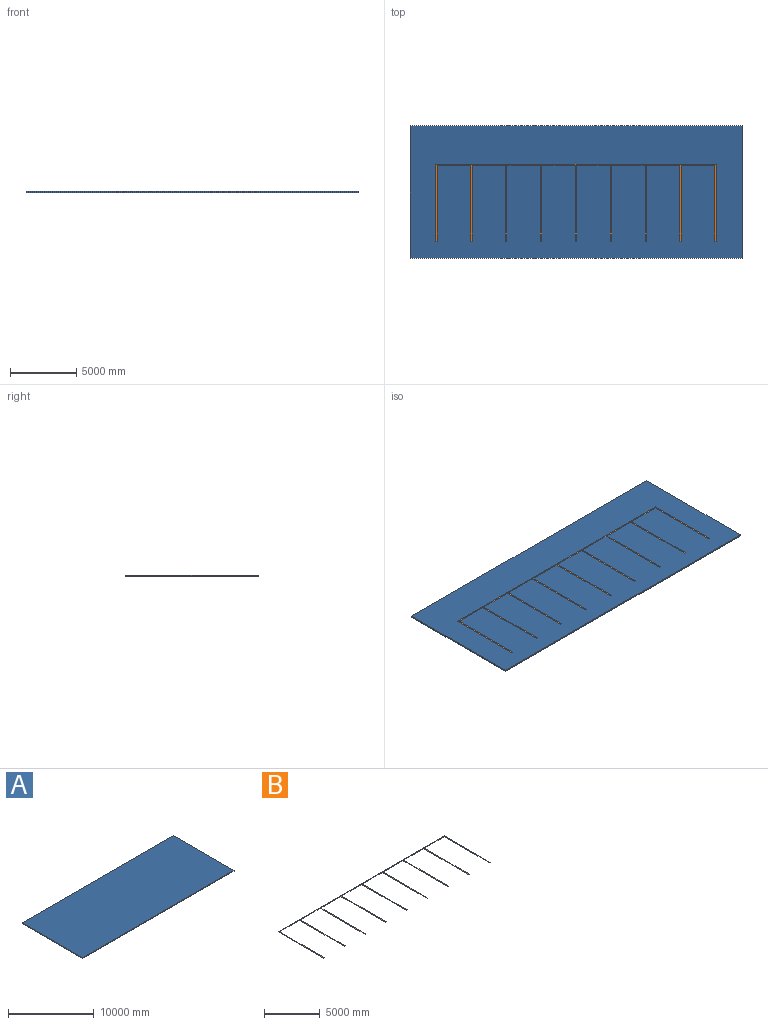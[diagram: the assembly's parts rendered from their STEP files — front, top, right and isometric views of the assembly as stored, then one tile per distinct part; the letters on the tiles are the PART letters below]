
ASSEMBLY  parts=2 mates=1
PART A: 6 faces, bbox 25000x10000x100 mm
  f0: plane 10000x100mm, normal (1,0,0), area 1000000mm2, adj f1,f3,f4,f5
  f1: plane 25000x100mm, normal (0,1,0), area 2500000mm2, adj f0,f2,f4,f5
  f2: plane 10000x100mm, normal (-1,0,0), area 1000000mm2, adj f1,f3,f4,f5
  f3: plane 25000x100mm, normal (0,-1,0), area 2500000mm2, adj f0,f2,f4,f5
  f4: plane 25000x10000mm, normal (0,0,1), area 250000000mm2, adj f0,f1,f2,f3
  f5: plane 25000x10000mm, normal (0,0,-1), area 250000000mm2, adj f0,f1,f2,f3
PART B: 38 faces, bbox 21100x5800x0.3 mm
  f0: plane 5800x0.25mm, normal (1,0,0), area 1450mm2, adj f1,f35,f36,f37
  f1: plane 21100x0.25mm, normal (0,1,0), area 5275mm2, adj f0,f2,f36,f37
  f2: plane 5800x0.25mm, normal (-1,0,0), area 1450mm2, adj f1,f3,f36,f37
  f3: plane 100x0.25mm, normal (0,-1,0), area 25mm2, adj f2,f4,f36,f37
  f4: plane 5700x0.25mm, normal (1,0,0), area 1425mm2, adj f3,f5,f36,f37
  f5: plane 2525x0.25mm, normal (0,-1,0), area 631.2mm2, adj f4,f6,f36,f37
  f6: plane 5700x0.25mm, normal (-1,0,0), area 1425mm2, adj f5,f7,f36,f37
  f7: plane 100x0.25mm, normal (0,-1,0), area 25mm2, adj f6,f8,f36,f37
  f8: plane 5700x0.25mm, normal (1,0,0), area 1425mm2, adj f7,f9,f36,f37
  f9: plane 2525x0.25mm, normal (0,-1,0), area 631.3mm2, adj f8,f10,f36,f37
  f10: plane 5700x0.25mm, normal (-1,0,0), area 1425mm2, adj f9,f11,f36,f37
  f11: plane 100x0.25mm, normal (0,-1,0), area 25mm2, adj f10,f12,f36,f37
  f12: plane 5700x0.25mm, normal (1,0,0), area 1425mm2, adj f11,f13,f36,f37
  f13: plane 2525x0.25mm, normal (0,-1,0), area 631.3mm2, adj f12,f14,f36,f37
  f14: plane 5700x0.25mm, normal (-1,0,0), area 1425mm2, adj f13,f15,f36,f37
  f15: plane 100x0.25mm, normal (0,-1,0), area 25mm2, adj f14,f16,f36,f37
  f16: plane 5700x0.25mm, normal (1,0,0), area 1425mm2, adj f15,f17,f36,f37
  f17: plane 2525x0.25mm, normal (0,-1,0), area 631.3mm2, adj f16,f18,f36,f37
  f18: plane 5700x0.25mm, normal (-1,0,0), area 1425mm2, adj f17,f19,f36,f37
  f19: plane 100x0.25mm, normal (0,-1,0), area 25mm2, adj f18,f20,f36,f37
  f20: plane 5700x0.25mm, normal (1,0,0), area 1425mm2, adj f19,f21,f36,f37
  f21: plane 2525x0.25mm, normal (0,-1,0), area 631.3mm2, adj f20,f22,f36,f37
  f22: plane 5700x0.25mm, normal (-1,0,0), area 1425mm2, adj f21,f23,f36,f37
  f23: plane 100x0.25mm, normal (0,-1,0), area 25mm2, adj f22,f24,f36,f37
  f24: plane 5700x0.25mm, normal (1,0,0), area 1425mm2, adj f23,f25,f36,f37
  f25: plane 2525x0.25mm, normal (0,-1,0), area 631.3mm2, adj f24,f26,f36,f37
  f26: plane 5700x0.25mm, normal (-1,0,0), area 1425mm2, adj f25,f27,f36,f37
  f27: plane 100x0.25mm, normal (0,-1,0), area 25mm2, adj f26,f28,f36,f37
  f28: plane 5700x0.25mm, normal (1,0,0), area 1425mm2, adj f27,f29,f36,f37
  f29: plane 2525x0.25mm, normal (0,-1,0), area 631.3mm2, adj f28,f30,f36,f37
  f30: plane 5700x0.25mm, normal (-1,0,0), area 1425mm2, adj f29,f31,f36,f37
  f31: plane 100x0.25mm, normal (0,-1,0), area 25mm2, adj f30,f32,f36,f37
  f32: plane 5700x0.25mm, normal (1,0,0), area 1425mm2, adj f31,f33,f36,f37
  f33: plane 2525x0.25mm, normal (0,-1,0), area 631.2mm2, adj f32,f34,f36,f37
  f34: plane 5700x0.25mm, normal (-1,0,0), area 1425mm2, adj f33,f35,f36,f37
  f35: plane 100x0.25mm, normal (0,-1,0), area 25mm2, adj f0,f34,f36,f37
  f36: plane 21100x5800mm, normal (0,0,1), area 7240000mm2, adj f0,f1,f2,f3,f4,f5,f6,f7
  f37: plane 21100x5800mm, normal (0,0,-1), area 7240000mm2, adj f0,f1,f2,f3,f4,f5,f6,f7
PLACE A t=(-532.83,6427.42,1011.11)mm
PLACE B t=(-532.83,5632.26,1111.11)mm
MATE parallel A.f4 <-> B.f37  axis (0,0,1) through (-532.83,6427.42,1111.11)mm
